# Revit family: Safety_Dock-Gate_Nova-Tech_Sentinel
name_source: partatom
category: Generic Models
revit_build: Autodesk Revit 2016 (Build: 20150714_1515(x64)
units: mm (PartAtom-declared; Revit-internal decimal feet)

## family parameters
Always vertical = No
Can host rebar = No
Cut with Voids When Loaded = No
OmniClass Number = 23.50.70.00
OmniClass Title = Loading Dock Equipment
Part Type = Normal
Room Calculation Point = No
Round Connector Dimension = Use Diameter
Shared = No
Work Plane-Based = Yes

## types (1)
- Safety_Dock-Gate_Nova-Tech_Sentinel
    Assembly Code = E1030300
    Capacity = 32000 lbs
    Default Elevation = 4' - 0"
    Description = Nova Technology Dock Product as Specified
    Expected Lifespan (Years) = 0
    Fixture Material = Metal - Nova - Yellow
    Keynote = 11160
    Maintenance Schedule (Months) = 0
    Manufacturer = Nova Technology
    Manufacturer Fax = 262-502-1511
    Manufacturer Website = http://www.novalocks.com
    Model = As Specified
    Product Data = http://arcat.com
    Revision = R1_04-2013
    Sales Information = http://www.novalocks.com
    Send Message = http://www.arcat.com
    Specification = http://arcat.com
    URL = http://www.novalocks.com
    Unit Depth = 0' - 10 1/2"
    Unit Height = 3' - 6 1/2"
    Unit Width = 8' - 0"
    Warranty Duration (Years) = 0
    bottombarlength = 5' - 0 1/2"
    bottombarsidelength = 4' - 9"
    topbarlength = 5' - 2 1/4"
    topbarsidelength = 4' - 9 1/4"

## geometry (parser evidence)
native form markers: Sweep x2
no freeform markers — native parametric forms only
